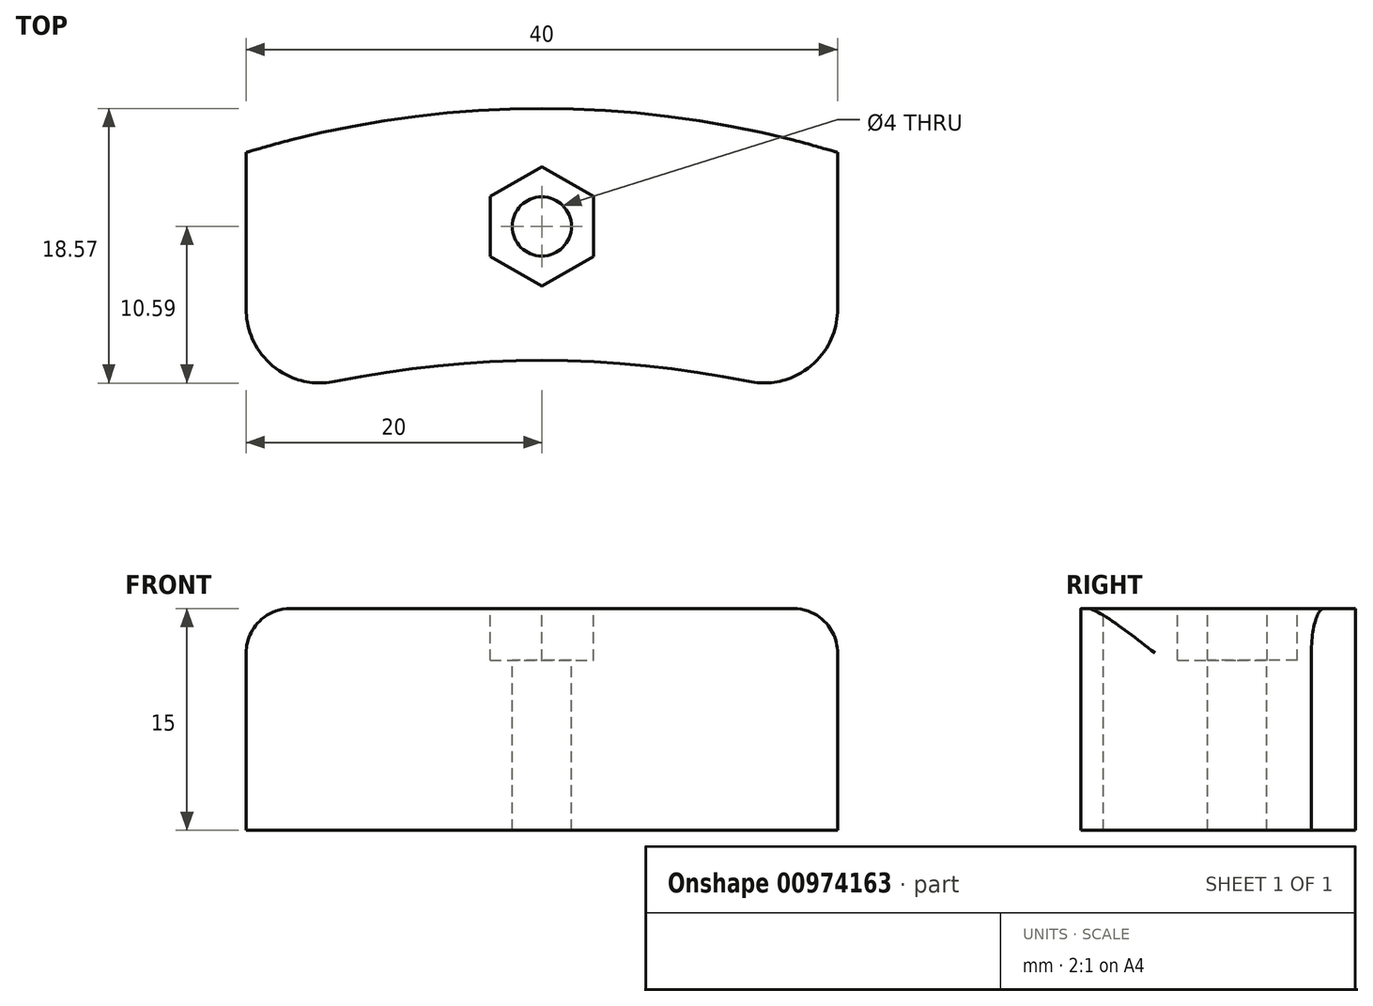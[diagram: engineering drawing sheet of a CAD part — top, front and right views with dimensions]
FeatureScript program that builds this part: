
annotation { "Feature Type Name" : "Feature", "Feature Type Description" : "" }
export const myFeature = defineFeature(function(context is Context, id is Id, definition is map)
    precondition{}
    {
        {
            var Q0;
            Q0=qCreatedBy(makeId("Top.planeOp"),FACE);
            var sketch = newSketch(context, id + "F0", { "sketchPlane" : qUnion([Q0])});
            skLineSegment(sketch, "E0.bottom", {"start": v(-20, 10) * mm, "end": v(20, 10) * mm});
            skLineSegment(sketch, "E0.top", {"start": v(-20, -10) * mm, "end": v(20, -10) * mm});
            skLineSegment(sketch, "E0.left", {"start": v(-20, 10) * mm, "end": v(-20, -10) * mm});
            skLineSegment(sketch, "E0.right", {"start": v(20, 10) * mm, "end": v(20, -10) * mm});
            skSolve(sketch);
        }
        {
            var Q0;
            Q0 = qSketchRegion(id + "F0", true);
            extrude(context, id + "F1", {"entities" : qUnion([Q0]), "oppositeDirection" : true, "depth" : 15 * mm, "offsetDistance" : 25 * mm});
        }
        {
            var Q0;
            Q0=makeQuery(id+"F1.opExtrude","CAP_FACE",FACE,{"disambiguationData":[OSD([sQuery(id+"F0.wireOp",EDGE,"E0.bottom"),sQuery(id+"F0.wireOp",EDGE,"E0.top"),sQuery(id+"F0.wireOp",EDGE,"E0.left"),sQuery(id+"F0.wireOp",EDGE,"E0.right")])],"isStart":true});
            var sketch = newSketch(context, id + "F2", { "sketchPlane" : qUnion([Q0])});
            skCircle(sketch, "E1.cCircle", {"center": v(0, 2) * mm, "radius": 3.5 * mm, "construction": true});
            skLineSegment(sketch, "E1.0", {"start": v(3.5, 4.02) * mm, "end": v(3.5, -0.02) * mm});
            skLineSegment(sketch, "E1.1", {"start": v(3.5, -0.02) * mm, "end": v(0, -2.04) * mm});
            skLineSegment(sketch, "E1.2", {"start": v(0, -2.04) * mm, "end": v(-3.5, -0.02) * mm});
            skLineSegment(sketch, "E1.3", {"start": v(-3.5, -0.02) * mm, "end": v(-3.5, 4.02) * mm});
            skLineSegment(sketch, "E1.4", {"start": v(-3.5, 4.02) * mm, "end": v(0, 6.04) * mm});
            skLineSegment(sketch, "E1.5", {"start": v(0, 6.04) * mm, "end": v(3.5, 4.02) * mm});
            skPoint(sketch, "E1.0.midPoint", {"position": v(3.5, 2) * mm});
            skSolve(sketch);
        }
        {
            var Q0;
            Q0 = qSketchRegion(id + "F2", true);
            extrude(context, id + "F3", {"entities" : qUnion([Q0]), "operationType" : NewBodyOperationType.REMOVE, "oppositeDirection" : true, "depth" : 3.5 * mm, "offsetDistance" : 25 * mm});
        }
        {
            var Q0;
            Q0=makeQuery(id+"F1.opExtrude","CAP_FACE",FACE,{"disambiguationData":[OSD([sQuery(id+"F0.wireOp",EDGE,"E0.bottom"),sQuery(id+"F0.wireOp",EDGE,"E0.top"),sQuery(id+"F0.wireOp",EDGE,"E0.left"),sQuery(id+"F0.wireOp",EDGE,"E0.right")])],"isStart":true});
            var sketch = newSketch(context, id + "F4", { "sketchPlane" : qUnion([Q0])});
            skArc(sketch, "E2", {"start": v(20, 7) * mm, "mid": v(0, 9.98) * mm, "end": v(-20, 7) * mm});
            skArc(sketch, "E3", {"start": v(20, -10) * mm, "mid": v(0, -7.06) * mm, "end": v(-20, -10) * mm});
            skLineSegment(sketch, "E4", {"start": v(-20, 7) * mm, "end": v(-20, 10) * mm});
            skLineSegment(sketch, "E5", {"start": v(-20, 10) * mm, "end": v(20, 10) * mm});
            skLineSegment(sketch, "E6", {"start": v(20, 10) * mm, "end": v(20, 7) * mm});
            skLineSegment(sketch, "E7", {"start": v(20, -10) * mm, "end": v(-20, -10) * mm});
            skSolve(sketch);
        }
        {
            var Q0;
            Q0 = qSketchRegion(id + "F4", true);
            extrude(context, id + "F5", {"entities" : qUnion([Q0]), "operationType" : NewBodyOperationType.REMOVE, "endBound" : BoundingType.THROUGH_ALL, "oppositeDirection" : true, "depth" : 25 * mm, "offsetDistance" : 25 * mm});
        }
        {
            var Q0;
            Q0=makeQuery(id+"F3.boolean.opBoolean","COPY",FACE,{"derivedFrom":makeQuery(id+"F3.opExtrude","CAP_FACE",FACE,{"disambiguationData":[OSD([sQuery(id+"F2.wireOp",EDGE,"E1.0"),sQuery(id+"F2.wireOp",EDGE,"E1.1"),sQuery(id+"F2.wireOp",EDGE,"E1.2"),sQuery(id+"F2.wireOp",EDGE,"E1.3"),sQuery(id+"F2.wireOp",EDGE,"E1.4"),sQuery(id+"F2.wireOp",EDGE,"E1.5")])],"isStart":false})});
            var sketch = newSketch(context, id + "F6", { "sketchPlane" : qUnion([Q0])});
            skCircle(sketch, "E8", {"center": v(0, 2) * mm, "radius": 2 * mm});
            skSolve(sketch);
        }
        {
            var Q0;
            Q0 = qSketchRegion(id + "F6", true);
            extrude(context, id + "F7", {"entities" : qUnion([Q0]), "operationType" : NewBodyOperationType.REMOVE, "endBound" : BoundingType.THROUGH_ALL, "oppositeDirection" : true, "depth" : 25 * mm, "offsetDistance" : 25 * mm});
        }
        {
            var Q0;
            Q0=makeQuery(id+"F5.boolean.opBoolean","COPY",EDGE,{"derivedFrom":makeQuery(id+"F5.opExtrude","SWEPT_EDGE",EDGE,{"disambiguationData":[OSD([sQuery(id+"F0.wireOp",EDGE,"E0.left"),sQuery(id+"F4.wireOp",EDGE,"E2"),sQuery(id+"F4.wireOp",EDGE,"E4")])]})});
            var Q1;
            Q1=makeQuery(id+"F5.boolean.opBoolean","COPY",EDGE,{"derivedFrom":makeQuery(id+"F5.opExtrude","SWEPT_EDGE",EDGE,{"disambiguationData":[OSD([sQuery(id+"F0.wireOp",EDGE,"E0.right"),sQuery(id+"F4.wireOp",EDGE,"E2"),sQuery(id+"F4.wireOp",EDGE,"E6")])]})});
            var Q2;
            {var subQ0=sQuery(id+"F0.wireOp",EDGE,"E0.left");Q2=makeQuery(id+"F5.boolean.opBoolean","MERGE",EDGE,{"derivedFrom":[makeQuery(id+"F1.opExtrude","SWEPT_EDGE",EDGE,{"disambiguationData":[OSD([sQuery(id+"F0.wireOp",EDGE,"E0.top"),subQ0])]})],"fromTools":[makeQuery(id+"F5.opExtrude","SWEPT_EDGE",EDGE,{"disambiguationData":[OSD([subQ0,sQuery(id+"F4.wireOp",EDGE,"E3"),sQuery(id+"F4.wireOp",EDGE,"E7")])]})]});}
            var Q3;
            {var subQ0=sQuery(id+"F0.wireOp",EDGE,"E0.right");Q3=makeQuery(id+"F5.boolean.opBoolean","MERGE",EDGE,{"derivedFrom":[makeQuery(id+"F1.opExtrude","SWEPT_EDGE",EDGE,{"disambiguationData":[OSD([sQuery(id+"F0.wireOp",EDGE,"E0.top"),subQ0])]})],"fromTools":[makeQuery(id+"F5.opExtrude","SWEPT_EDGE",EDGE,{"disambiguationData":[OSD([subQ0,sQuery(id+"F4.wireOp",EDGE,"E3"),sQuery(id+"F4.wireOp",EDGE,"E7")])]})]});}
            fillet(context, id + "F8", {"entities" : qUnion([Q0, Q1, Q2, Q3]), "radius" : 5 * mm, "tangentPropagation" : true, "allowEdgeOverflow" : false});
        }
        {
            var Q0;
            Q0=makeQuery(id+"F5.boolean.opBoolean","COPY",EDGE,{"derivedFrom":makeQuery(id+"F5.opExtrude","CAP_EDGE",EDGE,{"disambiguationData":[OSD([sQuery(id+"F4.wireOp",EDGE,"E2")])],"isStart":true})});
            var Q1;
            Q1=makeQuery(id+"F1.opExtrude","CAP_EDGE",EDGE,{"disambiguationData":[OSD([sQuery(id+"F0.wireOp",EDGE,"E0.left")])],"isStart":true});
            var Q2;
            Q2=makeQuery(id+"F1.opExtrude","CAP_EDGE",EDGE,{"disambiguationData":[OSD([sQuery(id+"F0.wireOp",EDGE,"E0.right")])],"isStart":true});
            var Q3;
            Q3=makeQuery(id+"F5.boolean.opBoolean","COPY",EDGE,{"derivedFrom":makeQuery(id+"F5.opExtrude","CAP_EDGE",EDGE,{"disambiguationData":[OSD([sQuery(id+"F4.wireOp",EDGE,"E3")])],"isStart":true})});
            fillet(context, id + "F9", {"entities" : qUnion([Q0, Q1, Q2, Q3]), "radius" : 3 * mm, "allowEdgeOverflow" : false});
        }
    });
